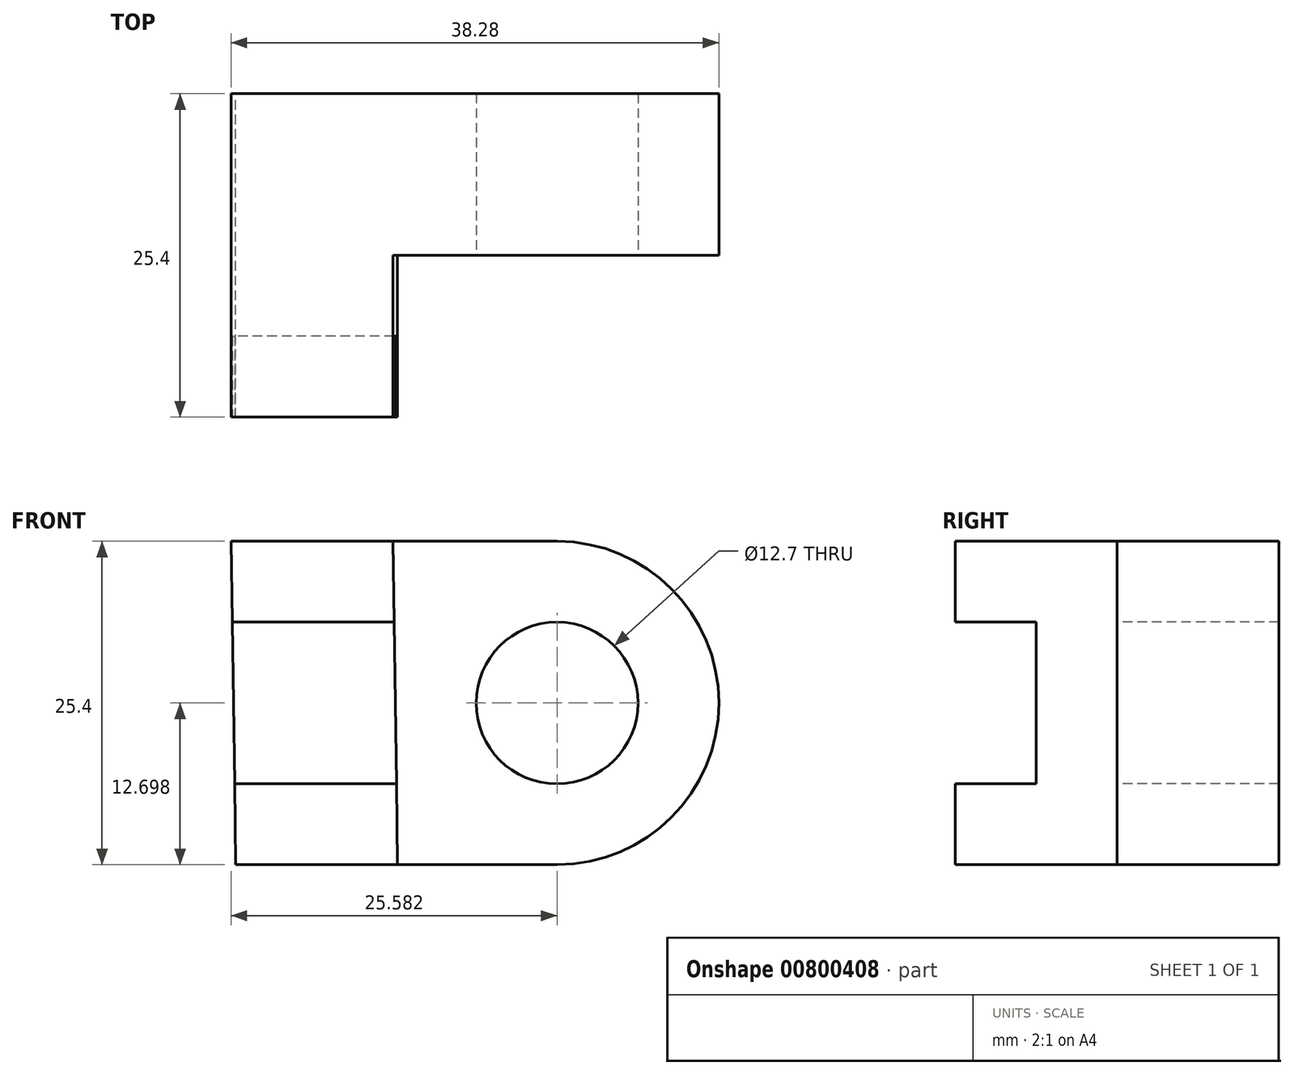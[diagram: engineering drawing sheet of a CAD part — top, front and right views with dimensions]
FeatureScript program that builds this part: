
annotation { "Feature Type Name" : "Feature", "Feature Type Description" : "" }
export const myFeature = defineFeature(function(context is Context, id is Id, definition is map)
    precondition{}
    {
        {
            var Q0;
            Q0=qCreatedBy(makeId("Front.planeOp"),FACE);
            var sketch = newSketch(context, id + "F0", { "sketchPlane" : qUnion([Q0])});
            skLineSegment(sketch, "E0", {"start": v(0.36, -0.12) * mm, "end": v(38.46, -0.12) * mm});
            skLineSegment(sketch, "E1", {"start": v(38.46, -0.12) * mm, "end": v(38.46, 25.28) * mm});
            skLineSegment(sketch, "E2", {"start": v(38.46, 25.28) * mm, "end": v(0, 25.28) * mm});
            skLineSegment(sketch, "E3", {"start": v(0, 25.28) * mm, "end": v(0.36, -0.12) * mm});
            skSolve(sketch);
        }
        {
            var Q0;
            Q0=makeQuery(id+"F0.imprint","IMPRINT",FACE,{"disambiguationData":[TD([[makeQuery(id+"F0.imprint","IMPRINT",EDGE,{"derivedFrom":sQuery(id+"F0.wireOp",EDGE,"E0")}),1.0]])]});
            extrude(context, id + "F1", {"entities" : qUnion([Q0]), "depth" : 25.4 * mm, "offsetDistance" : 25.4 * mm});
        }
        {
            var Q0;
            Q0=makeQuery(id+"F1.opExtrude","CAP_FACE",FACE,{"disambiguationData":[OSD([sQuery(id+"F0.wireOp",EDGE,"E0"),sQuery(id+"F0.wireOp",EDGE,"E1"),sQuery(id+"F0.wireOp",EDGE,"E2"),sQuery(id+"F0.wireOp",EDGE,"E3")])],"isStart":false});
            var sketch = newSketch(context, id + "F2", { "sketchPlane" : qUnion([Q0])});
            skLineSegment(sketch, "E4", {"start": v(0, 25.28) * mm, "end": v(12.7, 25.28) * mm, "construction": true});
            skLineSegment(sketch, "E5", {"start": v(12.7, 25.28) * mm, "end": v(13.06, -0.12) * mm});
            skSolve(sketch);
        }
        {
            var Q0;
            Q0 = qSketchRegion(id + "F2", true);
            var Q1;
            {var subQ0=sQuery(id+"F2.wireOp",EDGE,"E5");Q1=makeQuery(id+"F2.imprint","IMPRINT",FACE,{"disambiguationData":[TD([[makeQuery(id+"F2.imprint","IMPRINT",EDGE,{"derivedFrom":subQ0}),1.0]])]});}
            extrude(context, id + "F3", {"entities" : qUnion([Q0, Q1]), "operationType" : NewBodyOperationType.REMOVE, "oppositeDirection" : true, "depth" : 12.7 * mm, "offsetDistance" : 25.4 * mm});
        }
        {
            var Q0;
            Q0=makeQuery(id+"F1.opExtrude","CAP_FACE",FACE,{"disambiguationData":[OSD([sQuery(id+"F0.wireOp",EDGE,"E0"),sQuery(id+"F0.wireOp",EDGE,"E1"),sQuery(id+"F0.wireOp",EDGE,"E2"),sQuery(id+"F0.wireOp",EDGE,"E3")])],"isStart":false});
            var sketch = newSketch(context, id + "F4", { "sketchPlane" : qUnion([Q0])});
            skLineSegment(sketch, "E6", {"start": v(12.7, 25.28) * mm, "end": v(12.8, 18.93) * mm, "construction": true});
            skLineSegment(sketch, "E7", {"start": v(12.8, 18.93) * mm, "end": v(0.1, 18.93) * mm});
            skLineSegment(sketch, "E8", {"start": v(12.8, 18.93) * mm, "end": v(12.97, 6.23) * mm, "construction": true});
            skLineSegment(sketch, "E9", {"start": v(12.97, 6.23) * mm, "end": v(0.27, 6.23) * mm});
            skSolve(sketch);
        }
        {
            var Q0;
            Q0 = qSketchRegion(id + "F4", true);
            var Q1;
            {var subQ0=sQuery(id+"F4.wireOp",EDGE,"E7");Q1=makeQuery(id+"F4.imprint","IMPRINT",FACE,{"disambiguationData":[TD([[makeQuery(id+"F4.imprint","IMPRINT",EDGE,{"derivedFrom":subQ0}),1.0]])]});}
            extrude(context, id + "F5", {"entities" : qUnion([Q0, Q1]), "operationType" : NewBodyOperationType.REMOVE, "oppositeDirection" : true, "depth" : 6.35 * mm, "offsetDistance" : 25.4 * mm});
        }
        {
            var Q0;
            Q0=makeQuery(id+"F3.boolean.opBoolean","COPY",FACE,{"derivedFrom":makeQuery(id+"F3.opExtrude","CAP_FACE",FACE,{"disambiguationData":[OSD([sQuery(id+"F0.wireOp",EDGE,"E0"),sQuery(id+"F0.wireOp",EDGE,"E1"),sQuery(id+"F0.wireOp",EDGE,"E2"),sQuery(id+"F2.wireOp",EDGE,"E5")])],"isStart":false})});
            var sketch = newSketch(context, id + "F6", { "sketchPlane" : qUnion([Q0])});
            skArc(sketch, "E10", {"start": v(25.58, -0.12) * mm, "mid": v(38.28, 12.58) * mm, "end": v(25.58, 25.28) * mm});
            skPoint(sketch, "E10.startSnap0", {"position": v(25.58, 25.28) * mm});
            skCircle(sketch, "E11", {"center": v(25.58, 12.58) * mm, "radius": 6.35 * mm});
            skSolve(sketch);
        }
        {
            var Q0;
            Q0 = qSketchRegion(id + "F6", true);
            var Q1;
            {var subQ0=sQuery(id+"F6.wireOp",EDGE,"E10");Q1=makeQuery(id+"F6.imprint","IMPRINT",FACE,{"disambiguationData":[TD([[makeQuery(id+"F6.imprint","IMPRINT",EDGE,{"derivedFrom":subQ0}),-1.0]])]});}
            extrude(context, id + "F7", {"entities" : qUnion([Q0, Q1]), "operationType" : NewBodyOperationType.REMOVE, "endBound" : BoundingType.UP_TO_NEXT, "oppositeDirection" : true, "depth" : 25.4 * mm, "offsetDistance" : 25.4 * mm});
        }
    });
